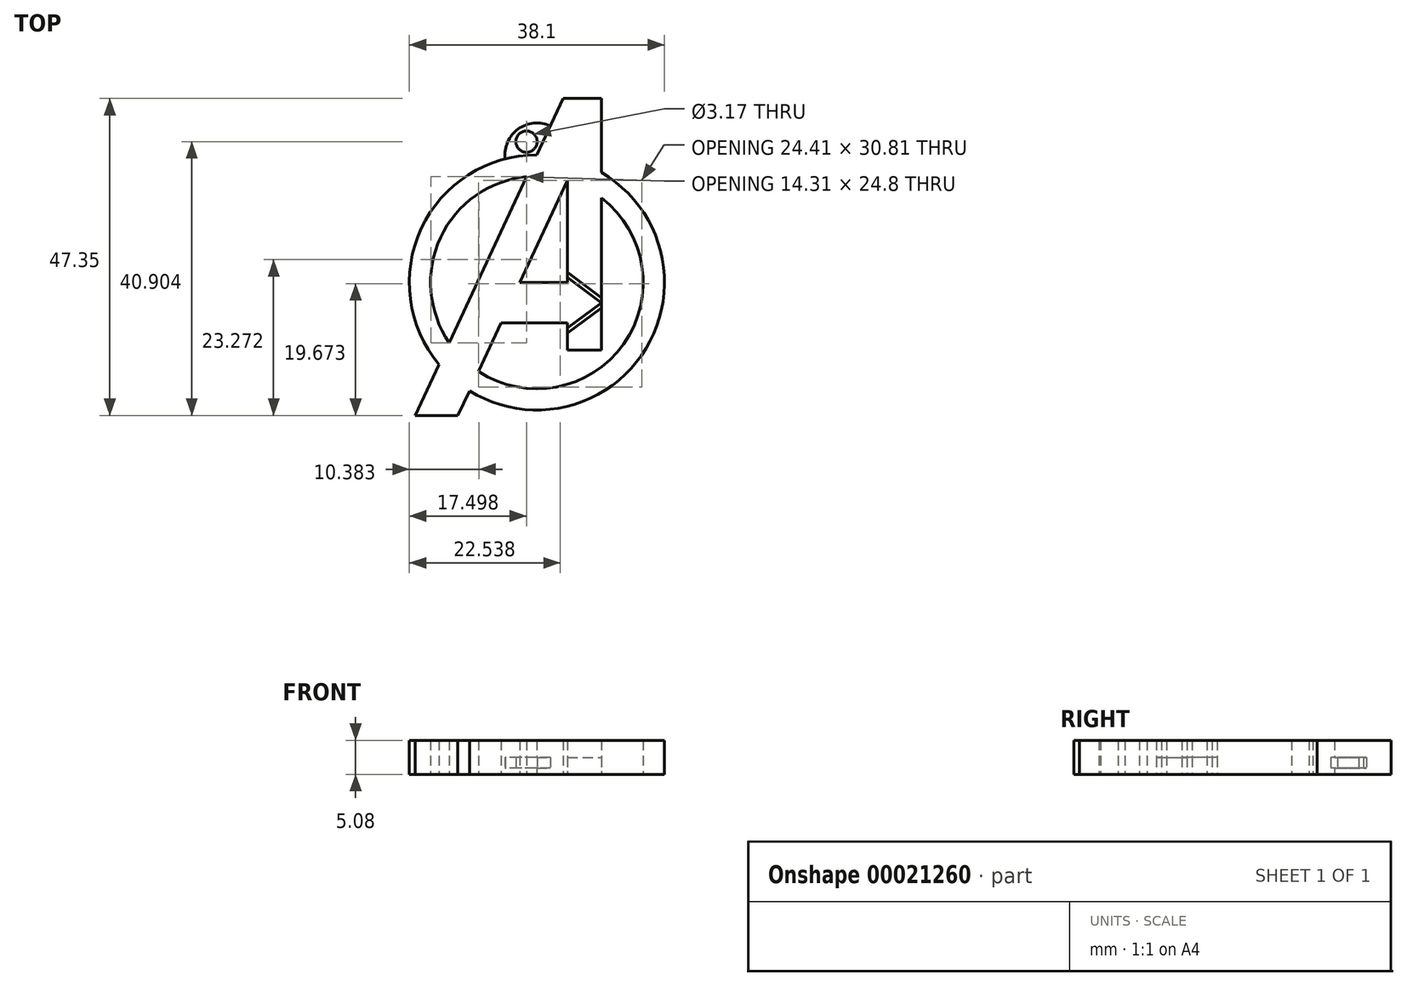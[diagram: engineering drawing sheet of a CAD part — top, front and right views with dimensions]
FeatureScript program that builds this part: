
annotation { "Feature Type Name" : "Feature", "Feature Type Description" : "" }
export const myFeature = defineFeature(function(context is Context, id is Id, definition is map)
    precondition{}
    {
        {
            var Q0;
            Q0=qCreatedBy(makeId("Top.planeOp"),FACE);
            var sketch = newSketch(context, id + "F0", { "sketchPlane" : qUnion([Q0])});
            skArc(sketch, "E0", {"start": v(0, 19.05) * mm, "mid": v(-17.27, 8.05) * mm, "end": v(-14.6, -12.25) * mm});
            skArc(sketch, "E1", {"start": v(-1.51, 15.8) * mm, "mid": v(-14.39, 6.7) * mm, "end": v(-13.08, -9) * mm});
            skLineSegment(sketch, "E2", {"start": v(0, 19.05) * mm, "end": v(-18.15, -19.87) * mm});
            skLineSegment(sketch, "E3", {"start": v(-18.15, -19.87) * mm, "end": v(-11.8, -19.87) * mm});
            skLineSegment(sketch, "E4", {"start": v(-11.8, -19.87) * mm, "end": v(-5.36, -6.05) * mm});
            skLineSegment(sketch, "E5", {"start": v(4.56, 15.2) * mm, "end": v(4.56, 0) * mm});
            skLineSegment(sketch, "E6", {"start": v(4.56, -10.12) * mm, "end": v(9.64, -10.12) * mm});
            skLineSegment(sketch, "E7", {"start": v(-14.6, -12.25) * mm, "end": v(-18.15, -19.87) * mm});
            skLineSegment(sketch, "E8", {"start": v(9.64, 12.61) * mm, "end": v(9.64, 27.48) * mm});
            skLineSegment(sketch, "E9", {"start": v(0, 19.05) * mm, "end": v(3.93, 27.48) * mm});
            skLineSegment(sketch, "E10", {"start": v(9.64, 27.48) * mm, "end": v(3.93, 27.48) * mm});
            skLineSegment(sketch, "E11", {"start": v(-5.36, -6.05) * mm, "end": v(4.56, -6.05) * mm});
            skLineSegment(sketch, "E12", {"start": v(-2.53, 0) * mm, "end": v(4.56, 0) * mm});
            skLineSegment(sketch, "E13.trimOffspring", {"start": v(4.56, -6.05) * mm, "end": v(4.56, -10.12) * mm});
            skLineSegment(sketch, "E14.trimOffspring", {"start": v(-2.53, 0) * mm, "end": v(4.56, 15.2) * mm});
            skArc(sketch, "E15.trimOffspring", {"start": v(-8.72, -13.27) * mm, "mid": v(12.95, -9.18) * mm, "end": v(9.64, 12.61) * mm});
            skArc(sketch, "E16.trimOffspring", {"start": v(-10.07, -16.17) * mm, "mid": v(16.3, -9.86) * mm, "end": v(9.64, 16.43) * mm});
            skArc(sketch, "E17", {"start": v(2.01, 23.37) * mm, "mid": v(-2.8, 22.9) * mm, "end": v(-4.73, 18.45) * mm});
            skCircle(sketch, "E18", {"center": v(-1.55, 21.03) * mm, "radius": 1.59 * mm});
            skLineSegment(sketch, "E19", {"start": v(4.56, 0) * mm, "end": v(4.56, 0.76) * mm});
            skLineSegment(sketch, "E20", {"start": v(4.56, 0.76) * mm, "end": v(4.56, 1.52) * mm});
            skLineSegment(sketch, "E21", {"start": v(4.56, -6.05) * mm, "end": v(4.56, -6.81) * mm});
            skLineSegment(sketch, "E22", {"start": v(4.56, -6.81) * mm, "end": v(4.56, -7.58) * mm});
            skLineSegment(sketch, "E23", {"start": v(4.56, 0.76) * mm, "end": v(9.64, -3.03) * mm});
            skLineSegment(sketch, "E24", {"start": v(4.56, -6.81) * mm, "end": v(9.64, -3.03) * mm});
            skLineSegment(sketch, "E25", {"start": v(4.56, 1.52) * mm, "end": v(9.64, -2.26) * mm});
            skLineSegment(sketch, "E26", {"start": v(4.56, -7.58) * mm, "end": v(9.64, -3.79) * mm});
            skPoint(sketch, "E27.trimOffspring.start.orphan", {"position": v(9.64, -6.05) * mm});
            skPoint(sketch, "E28.end.orphan", {"position": v(9.64, 0) * mm});
            skLineSegment(sketch, "E29", {"start": v(9.64, 12.61) * mm, "end": v(9.64, -10.12) * mm});
            skLineSegment(sketch, "E30", {"start": v(4.56, 1.14) * mm, "end": v(9.64, -2.65) * mm});
            skLineSegment(sketch, "E31", {"start": v(4.56, -7.2) * mm, "end": v(9.64, -3.4) * mm});
            skLineSegment(sketch, "E32", {"start": v(-11.8, -19.87) * mm, "end": v(25.13, -19.87) * mm});
            skLineSegment(sketch, "E33", {"start": v(9.64, 27.48) * mm, "end": v(25.13, 27.48) * mm});
            skLineSegment(sketch, "E34", {"start": v(25.13, 27.48) * mm, "end": v(25.13, -19.87) * mm});
            skLineSegment(sketch, "E35", {"start": v(-19.05, 0) * mm, "end": v(-19.05, -24.18) * mm});
            skLineSegment(sketch, "E36", {"start": v(-19.05, -24.18) * mm, "end": v(19.05, -24.18) * mm});
            skLineSegment(sketch, "E37", {"start": v(19.05, 0) * mm, "end": v(19.05, -24.18) * mm});
            skSolve(sketch);
        }
        {
            var Q0;
            {var subQ2=sQuery(id+"F0.wireOp",EDGE,"E0");Q0=makeQuery(id+"F0.imprint","IMPRINT",FACE,{"disambiguationData":[TD([[makeQuery(id+"F0.imprint","IMPRINT",EDGE,{"derivedFrom":subQ2}),1.0]])]});}
            var Q1;
            {var subQ9=sQuery(id+"F0.wireOp",EDGE,"E3");Q1=makeQuery(id+"F0.imprint","IMPRINT",FACE,{"disambiguationData":[TD([[makeQuery(id+"F0.imprint","IMPRINT",EDGE,{"derivedFrom":subQ9}),1.0]])]});}
            var Q2;
            {var subQ0=sQuery(id+"F0.wireOp",EDGE,"E15.trimOffspring");Q2=makeQuery(id+"F0.imprint","IMPRINT",FACE,{"disambiguationData":[TD([[makeQuery(id+"F0.imprint","IMPRINT",EDGE,{"derivedFrom":subQ0}),-1.0]])]});}
            var Q3;
            Q3=makeQuery(id+"F0.imprint","IMPRINT",FACE,{"disambiguationData":[TD([[makeQuery(id+"F0.imprint","IMPRINT",EDGE,{"derivedFrom":sQuery(id+"F0.wireOp",EDGE,"E6")}),1.0]])]});
            var Q4;
            {var subQ1=sQuery(id+"F0.wireOp",EDGE,"406db947-73c3-418f-ad74-710f48655b45");Q4=makeQuery(id+"F0.imprint","IMPRINT",FACE,{"disambiguationData":[TD([[makeQuery(id+"F0.imprint","IMPRINT",EDGE,{"derivedFrom":subQ1}),-1.0]])]});}
            var Q5;
            {var subQ2=sQuery(id+"F0.wireOp",EDGE,"08405404-7948-4caf-93e0-b9b2559490a3");Q5=makeQuery(id+"F0.imprint","IMPRINT",FACE,{"disambiguationData":[TD([[makeQuery(id+"F0.imprint","IMPRINT",EDGE,{"derivedFrom":subQ2}),1.0]])]});}
            var Q6;
            {var subQ2=sQuery(id+"F0.wireOp",EDGE,"49d6b685-f15b-4148-abe2-4aacc5afd56f");Q6=makeQuery(id+"F0.imprint","IMPRINT",FACE,{"disambiguationData":[TD([[makeQuery(id+"F0.imprint","IMPRINT",EDGE,{"derivedFrom":subQ2}),1.0]])]});}
            var Q7;
            {var subQ2=sQuery(id+"F0.wireOp",EDGE,"e047c4b4-439f-4a13-8362-1945e49fde9b");Q7=makeQuery(id+"F0.imprint","IMPRINT",FACE,{"disambiguationData":[TD([[makeQuery(id+"F0.imprint","IMPRINT",EDGE,{"derivedFrom":subQ2}),1.0]])]});}
            extrude(context, id + "F1", {"entities" : qUnion([Q0, Q1, Q2, Q3, Q4, Q5, Q6, Q7]), "depth" : 2.54 * mm});
        }
        {
            var Q0;
            {var subQ1=sQuery(id+"F0.wireOp",EDGE,"E15.trimOffspring");Q0=makeQuery(id+"F0.imprint","IMPRINT",FACE,{"disambiguationData":[TD([[makeQuery(id+"F0.imprint","IMPRINT",EDGE,{"derivedFrom":subQ1}),-1.0]])]});}
            var Q1;
            {var subQ1=sQuery(id+"F0.wireOp",EDGE,"E1");Q1=makeQuery(id+"F0.imprint","IMPRINT",FACE,{"disambiguationData":[TD([[makeQuery(id+"F0.imprint","IMPRINT",EDGE,{"derivedFrom":subQ1}),-1.0]])]});}
            var Q2;
            {var subQ9=sQuery(id+"F0.wireOp",EDGE,"E3");Q2=makeQuery(id+"F0.imprint","IMPRINT",FACE,{"disambiguationData":[TD([[makeQuery(id+"F0.imprint","IMPRINT",EDGE,{"derivedFrom":subQ9}),1.0]])]});}
            var Q3;
            {var subQ2=sQuery(id+"F0.wireOp",EDGE,"E6");Q3=makeQuery(id+"F0.imprint","IMPRINT",FACE,{"disambiguationData":[TD([[makeQuery(id+"F0.imprint","IMPRINT",EDGE,{"derivedFrom":subQ2}),1.0]])]});}
            extrude(context, id + "F2", {"entities" : qUnion([Q0, Q1, Q2, Q3]), "operationType" : NewBodyOperationType.ADD, "oppositeDirection" : true, "depth" : 2.54 * mm});
        }
        {
            var Q0;
            {var subQ0=sQuery(id+"F0.wireOp",EDGE,"E17");Q0=makeQuery(id+"F0.imprint","IMPRINT",FACE,{"disambiguationData":[TD([[makeQuery(id+"F0.imprint","IMPRINT",EDGE,{"derivedFrom":subQ0}),1.0]])]});}
            extrude(context, id + "F3", {"entities" : qUnion([Q0]), "operationType" : NewBodyOperationType.ADD, "depth" : 0.07 / 50.8 * mm});
        }
        {
            var Q0;
            {var subQ0=sQuery(id+"F0.wireOp",EDGE,"E17");Q0=makeQuery(id+"F0.imprint","IMPRINT",FACE,{"disambiguationData":[TD([[makeQuery(id+"F0.imprint","IMPRINT",EDGE,{"derivedFrom":subQ0}),1.0]])]});}
            extrude(context, id + "F4", {"entities" : qUnion([Q0]), "operationType" : NewBodyOperationType.ADD, "oppositeDirection" : true, "depth" : 0.07 / 50.8 * mm});
        }
        {
            var Q0;
            {var subQ2=sQuery(id+"F0.wireOp",EDGE,"E25");Q0=makeQuery(id+"F0.imprint","IMPRINT",FACE,{"disambiguationData":[TD([[makeQuery(id+"F0.imprint","IMPRINT",EDGE,{"derivedFrom":subQ2}),-1.0]])]});}
            var Q1;
            {var subQ2=sQuery(id+"F0.wireOp",EDGE,"E23");Q1=makeQuery(id+"F0.imprint","IMPRINT",FACE,{"disambiguationData":[TD([[makeQuery(id+"F0.imprint","IMPRINT",EDGE,{"derivedFrom":subQ2}),1.0]])]});}
            var Q2;
            {var subQ2=sQuery(id+"F0.wireOp",EDGE,"E24");Q2=makeQuery(id+"F0.imprint","IMPRINT",FACE,{"disambiguationData":[TD([[makeQuery(id+"F0.imprint","IMPRINT",EDGE,{"derivedFrom":subQ2}),-1.0]])]});}
            var Q3;
            {var subQ2=sQuery(id+"F0.wireOp",EDGE,"E26");Q3=makeQuery(id+"F0.imprint","IMPRINT",FACE,{"disambiguationData":[TD([[makeQuery(id+"F0.imprint","IMPRINT",EDGE,{"derivedFrom":subQ2}),1.0]])]});}
            extrude(context, id + "F5", {"entities" : qUnion([Q0, Q1, Q2, Q3]), "operationType" : NewBodyOperationType.ADD, "depth" : 0.17 / 50.8 * mm});
        }
        {
            var Q0;
            {var subQ2=sQuery(id+"F0.wireOp",EDGE,"E23");Q0=makeQuery(id+"F0.imprint","IMPRINT",FACE,{"disambiguationData":[TD([[makeQuery(id+"F0.imprint","IMPRINT",EDGE,{"derivedFrom":subQ2}),1.0]])]});}
            var Q1;
            {var subQ2=sQuery(id+"F0.wireOp",EDGE,"E25");Q1=makeQuery(id+"F0.imprint","IMPRINT",FACE,{"disambiguationData":[TD([[makeQuery(id+"F0.imprint","IMPRINT",EDGE,{"derivedFrom":subQ2}),-1.0]])]});}
            var Q2;
            {var subQ2=sQuery(id+"F0.wireOp",EDGE,"E24");Q2=makeQuery(id+"F0.imprint","IMPRINT",FACE,{"disambiguationData":[TD([[makeQuery(id+"F0.imprint","IMPRINT",EDGE,{"derivedFrom":subQ2}),-1.0]])]});}
            var Q3;
            {var subQ2=sQuery(id+"F0.wireOp",EDGE,"E26");Q3=makeQuery(id+"F0.imprint","IMPRINT",FACE,{"disambiguationData":[TD([[makeQuery(id+"F0.imprint","IMPRINT",EDGE,{"derivedFrom":subQ2}),1.0]])]});}
            extrude(context, id + "F6", {"entities" : qUnion([Q0, Q1, Q2, Q3]), "operationType" : NewBodyOperationType.ADD, "oppositeDirection" : true, "depth" : 0.17 / 50.8 * mm});
        }
        {
            var Q0;
            Q0=makeQuery(id+"F4.opExtrude","CAP_FACE",FACE,{"disambiguationData":[OSD([sQuery(id+"F0.wireOp",EDGE,"E0"),sQuery(id+"F0.wireOp",EDGE,"E9"),sQuery(id+"F0.wireOp",EDGE,"E17"),sQuery(id+"F0.wireOp",EDGE,"E18")])],"isStart":false});
            extrude(context, id + "F7", {"entities" : qUnion([Q0]), "operationType" : NewBodyOperationType.ADD, "depth" : 1.59 * mm});
        }
    });
